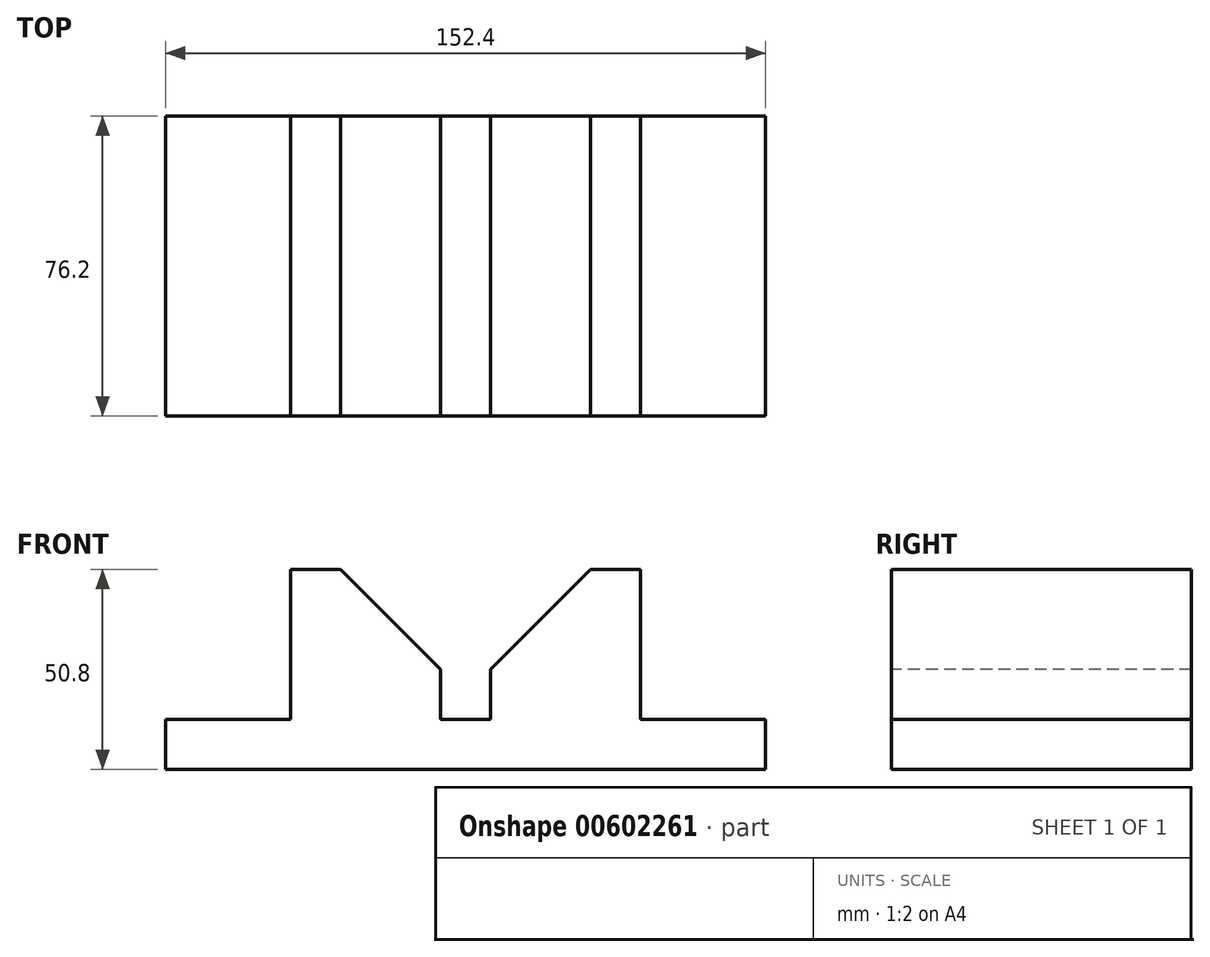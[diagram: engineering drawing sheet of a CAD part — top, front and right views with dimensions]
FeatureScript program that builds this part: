
annotation { "Feature Type Name" : "Feature", "Feature Type Description" : "" }
export const myFeature = defineFeature(function(context is Context, id is Id, definition is map)
    precondition{}
    {
        {
            var Q0;
            Q0=qCreatedBy(makeId("Front.planeOp"),FACE);
            var sketch = newSketch(context, id + "F0", { "sketchPlane" : qUnion([Q0])});
            skLineSegment(sketch, "E0.bottom", {"start": v(194.37, 0) * mm, "end": v(346.77, 0) * mm});
            skLineSegment(sketch, "E0.top", {"start": v(226.12, 50.8) * mm, "end": v(238.82, 50.8) * mm});
            skLineSegment(sketch, "E0.left", {"start": v(194.37, 0) * mm, "end": v(194.37, 12.7) * mm});
            skLineSegment(sketch, "E1", {"start": v(346.77, 0) * mm, "end": v(346.77, 12.7) * mm});
            skLineSegment(sketch, "E2", {"start": v(346.77, 12.7) * mm, "end": v(315.02, 12.7) * mm});
            skLineSegment(sketch, "E3", {"start": v(315.02, 12.7) * mm, "end": v(315.02, 50.8) * mm});
            skLineSegment(sketch, "E4", {"start": v(315.02, 50.8) * mm, "end": v(302.32, 50.8) * mm});
            skLineSegment(sketch, "E5", {"start": v(194.37, 12.7) * mm, "end": v(226.12, 12.7) * mm});
            skLineSegment(sketch, "E6", {"start": v(226.12, 12.7) * mm, "end": v(226.12, 50.8) * mm});
            skLineSegment(sketch, "E7", {"start": v(276.92, 12.7) * mm, "end": v(276.92, 25.4) * mm});
            skLineSegment(sketch, "E8", {"start": v(264.22, 12.7) * mm, "end": v(264.22, 25.4) * mm});
            skLineSegment(sketch, "E9", {"start": v(264.22, 25.4) * mm, "end": v(238.82, 50.8) * mm});
            skLineSegment(sketch, "E10", {"start": v(276.92, 25.4) * mm, "end": v(302.32, 50.8) * mm});
            skLineSegment(sketch, "E11", {"start": v(264.22, 12.7) * mm, "end": v(276.92, 12.7) * mm});
            skPoint(sketch, "E12.orphan", {"position": v(346.77, 50.8) * mm});
            skSolve(sketch);
        }
        {
            var Q0;
            Q0 = qSketchRegion(id + "F0", true);
            extrude(context, id + "F1", {"entities" : qUnion([Q0]), "oppositeDirection" : true, "depth" : 76.2 * mm, "offsetDistance" : 25.4 * mm});
        }
    });
